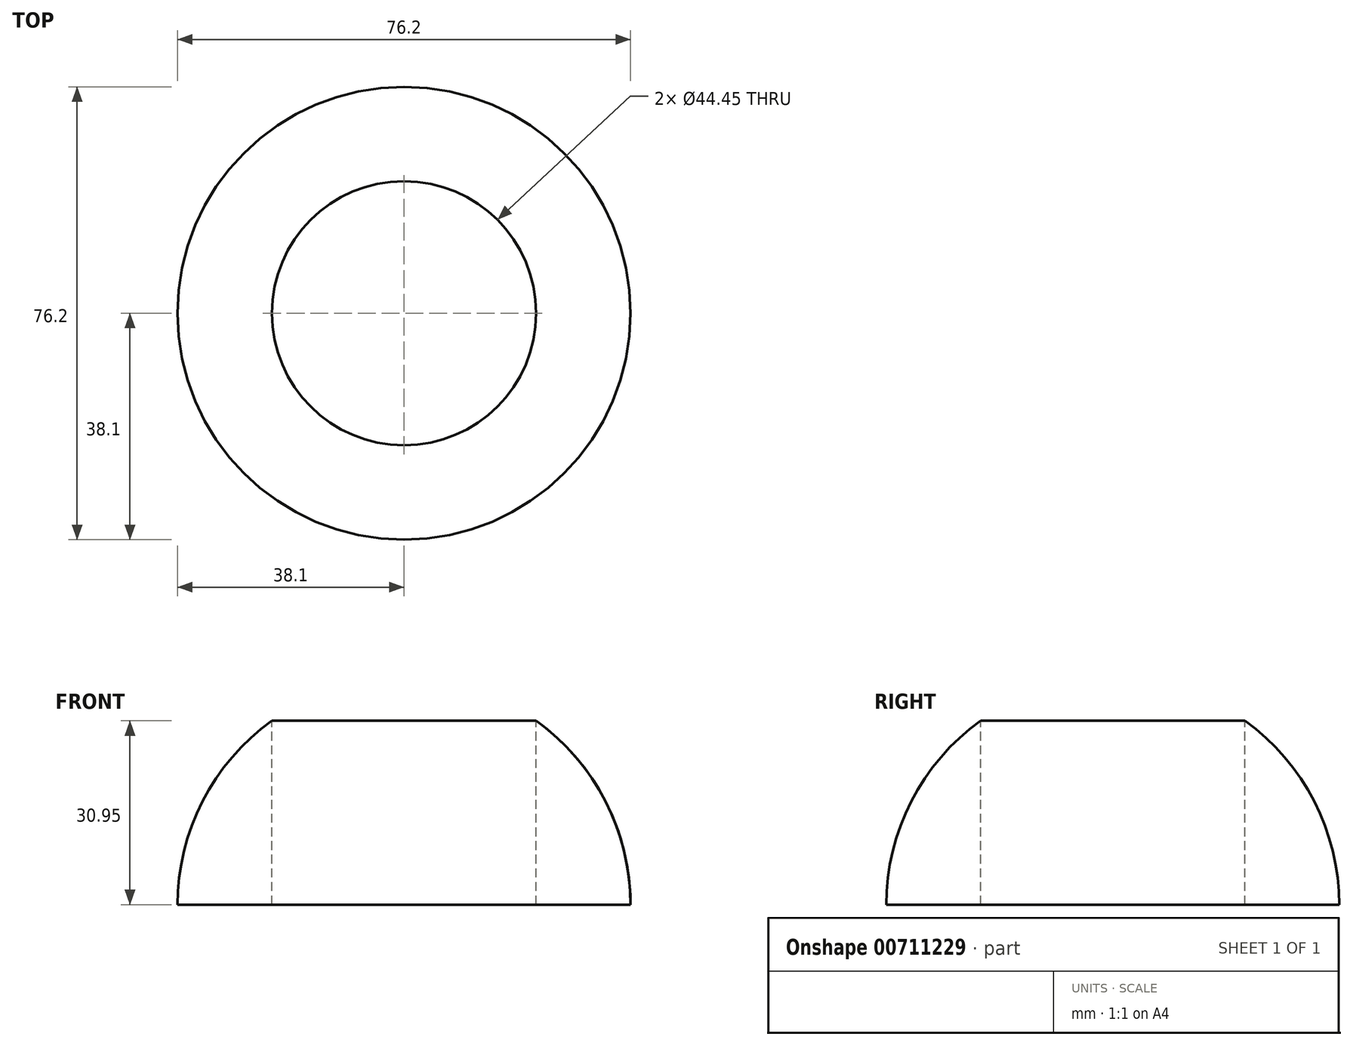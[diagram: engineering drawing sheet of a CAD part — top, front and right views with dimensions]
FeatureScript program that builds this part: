
annotation { "Feature Type Name" : "Feature", "Feature Type Description" : "" }
export const myFeature = defineFeature(function(context is Context, id is Id, definition is map)
    precondition{}
    {
        {
            var Q0;
            Q0=qCreatedBy(makeId("Top.planeOp"),FACE);
            var sketch = newSketch(context, id + "F0", { "sketchPlane" : qUnion([Q0])});
            skCircle(sketch, "E0", {"center": v(0, 0) * mm, "radius": 38.1 * mm});
            skSolve(sketch);
        }
        {
            var Q0;
            Q0=makeQuery(id+"F0.imprint","IMPRINT",FACE,{"disambiguationData":[TD([[makeQuery(id+"F0.imprint","IMPRINT",EDGE,{"derivedFrom":sQuery(id+"F0.wireOp",EDGE,"E0")}),1.0]])]});
            extrude(context, id + "F1", {"entities" : qUnion([Q0]), "depth" : 38.1 * mm, "offsetDistance" : 25.4 * mm});
        }
        {
            var Q0;
            Q0=makeQuery(id+"F1.opExtrude","CAP_FACE",FACE,{"disambiguationData":[OSD([sQuery(id+"F0.wireOp",EDGE,"E0")])],"isStart":false});
            fillet(context, id + "F2", {"entities" : qUnion([Q0]), "radius" : 38.1 * mm, "tangentPropagation" : true, "allowEdgeOverflow" : false});
        }
        {
            var Q0;
            Q0=qCreatedBy(makeId("Top.planeOp"),FACE);
            var sketch = newSketch(context, id + "F3", { "sketchPlane" : qUnion([Q0])});
            skCircle(sketch, "E1", {"center": v(0, 0) * mm, "radius": 22.23 * mm});
            skSolve(sketch);
        }
        {
            var Q0;
            Q0=makeQuery(id+"F3.imprint","IMPRINT",FACE,{"disambiguationData":[TD([[makeQuery(id+"F3.imprint","IMPRINT",EDGE,{"derivedFrom":sQuery(id+"F3.wireOp",EDGE,"E1")}),1.0]])]});
            extrude(context, id + "F4", {"entities" : qUnion([Q0]), "operationType" : NewBodyOperationType.REMOVE, "depth" : 151.38 * mm, "offsetDistance" : 25.4 * mm, "hasDraft" : true, "draftAngle" : 0 * degree});
        }
    });
